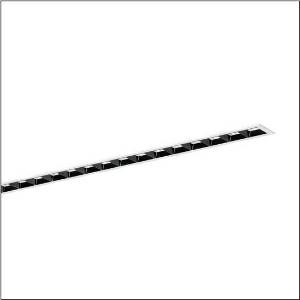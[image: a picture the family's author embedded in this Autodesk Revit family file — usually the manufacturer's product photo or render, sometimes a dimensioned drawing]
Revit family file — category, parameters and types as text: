
# Revit family: silica_r__21_51mx11tctaw_2435
name_source: partatom
category: Lighting Fixtures
units: mm (PartAtom-declared; Revit-internal decimal feet)

## family parameters
Cut with Voids When Loaded = No
Host = Face
Light Source = No
Part Type = Normal
Room Calculation Point = No
Round Connector Dimension = Use Diameter
Shared = No

## types (1)
- --- (1 x LED, 9300 lm, 80.5 W, 6500K)
    Apparent Load = 81 VA
    CIE Flux Codes = 85 99 100 100 100
    Color Rendering = 80
    Color Temperature = 6500K
    Default Elevation = 1800 mm
    Description = Silica® 21, office luminaire, primary light control with darklight reflector, of PMMA, black, CAT 2 (L<= 3000cd/m²), light emission: direct distribution, primary light characteristic: symmetric, installation type: recessed, LED, rated luminous flux: 9.300lm, luminous efficacy: 110lm/W, light colour: 8tw, colour temperature: 2700..6500K, with terminal, 3+2-pole, max. 2.5mm², mains connection: 220..240V, AC, 50/60Hz, rated input power: 84.6W, luminaire housing, of aluminium, traffic white (RAL 9016), length: 3.028mm, width: 79mm, height: 53mm, protection rating (complete): IP20, insulation class (complete): insulation class I (protective earthing), certification: CE, permissible operating ambient temperature: 0..+35°C, standard: EN 50419, packaging unit: 1 piece
    Height = 0 mm  [stored 0 ft]
    Lamp = 1 x LED
    Lamp Light Flux = 9300 lm
    Lamp Power = 80.5 W
    Lamp count = 1
    Length = 3027 mm
    Luminous efficacy = 116 lm/W
    Manufacturer = Siteco
    ModVariant = No
    Model = 51MX11TCTAW
    Mounting Place = Ceiling
    Mounting Type = Recessed
    Number of Poles = 1
    OnlyDefault = Yes
    Power Factor = 1
    Product Name = Silica® 21
    Product group = office luminaire | ceiling recessed
    ProductGroupID = 400
    Protection Class = Protection class I
    Protection Degree = IP 20
    RLX_Detail_Level = 1
    RlxData = <blob elided: 60133 chars, md5=521474b9>
    Socket = socket
    Standby Power = 0 W
    System Light Flux = 9300 lm
    System Power = 81 W
    Type Comments = individual setting
    Type Image = l_1251632.jpg
    URL = http://relux.com
    VarID = @adj_046185
    Voltage = 0 V
    Weight = 0.00 kg
    Width = 79 mm

note: [stored X ft] marks values corroborated as IEEE doubles in the binary element streams (Revit-internal decimal feet)

## geometry (parser evidence)
native form markers: Blend x4, Sweep x12
no freeform markers — native parametric forms only
